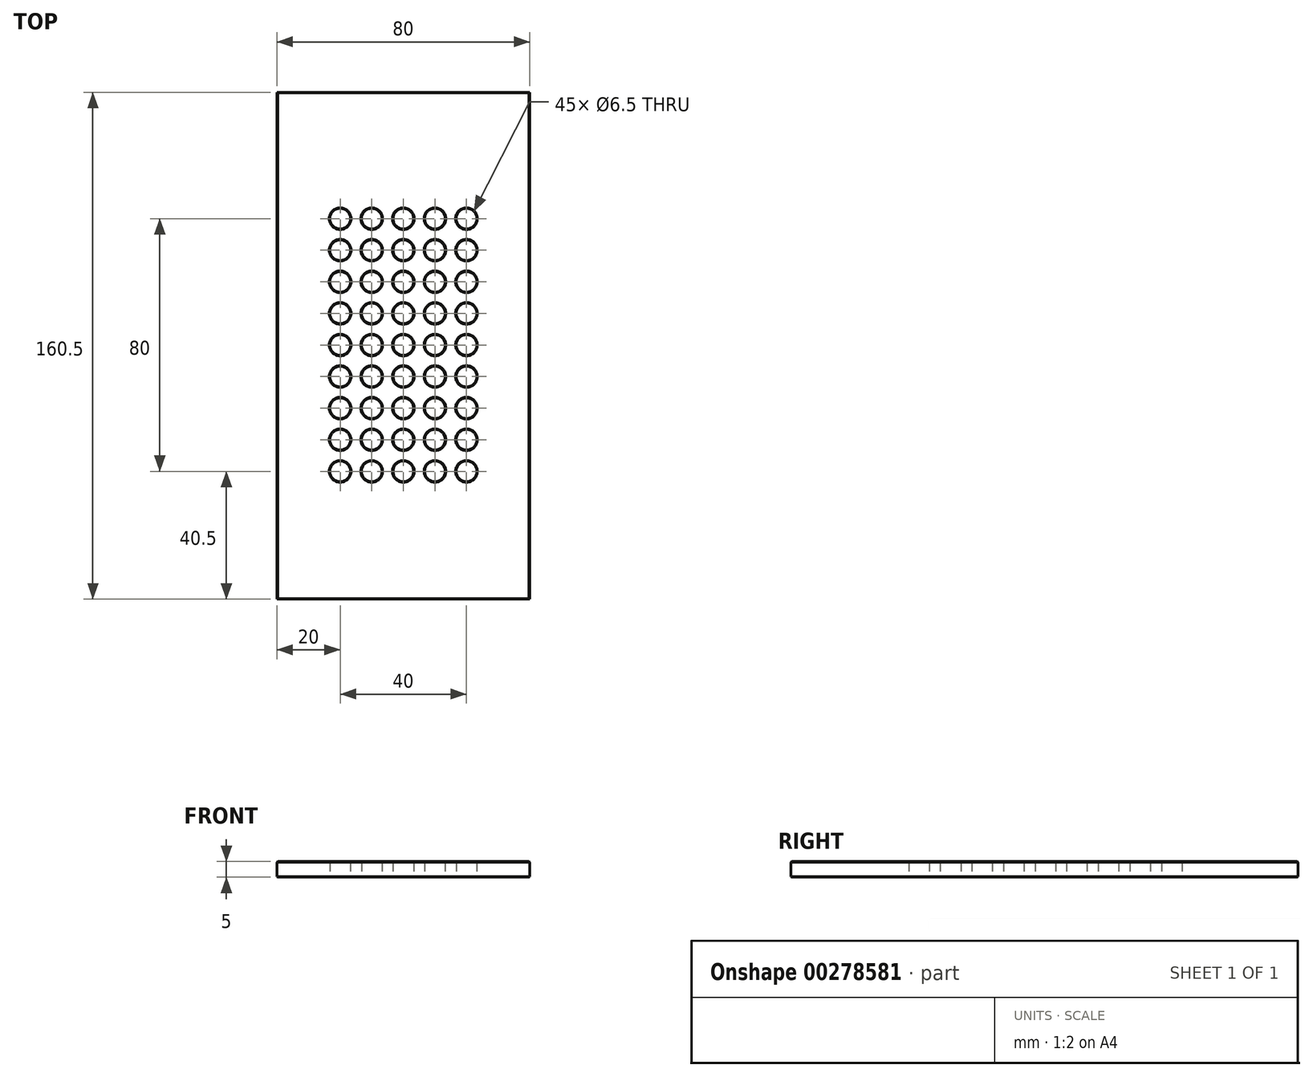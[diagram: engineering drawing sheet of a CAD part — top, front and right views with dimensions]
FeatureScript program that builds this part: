
annotation { "Feature Type Name" : "Feature", "Feature Type Description" : "" }
export const myFeature = defineFeature(function(context is Context, id is Id, definition is map)
    precondition{}
    {
        {
            var Q0;
            Q0=qCreatedBy(makeId("Top.planeOp"),FACE);
            var sketch = newSketch(context, id + "F0", { "sketchPlane" : qUnion([Q0])});
            skLineSegment(sketch, "E0.bottom", {"start": v(40, -80.25) * mm, "end": v(-40, -80.25) * mm});
            skLineSegment(sketch, "E0.top", {"start": v(40, 80.25) * mm, "end": v(-40, 80.25) * mm});
            skLineSegment(sketch, "E0.left", {"start": v(40, -80.25) * mm, "end": v(40, 80.25) * mm});
            skLineSegment(sketch, "E0.right", {"start": v(-40, -80.25) * mm, "end": v(-40, 80.25) * mm});
            skPoint(sketch, "E0.middle", {"position": v(0, 0) * mm});
            skLineSegment(sketch, "E1", {"start": v(-40, -50.25) * mm, "end": v(40, -50.25) * mm, "construction": true});
            skLineSegment(sketch, "E2", {"start": v(-40, 50.25) * mm, "end": v(40, 50.25) * mm, "construction": true});
            skLineSegment(sketch, "E3", {"start": v(0, 80.25) * mm, "end": v(0, -80.25) * mm, "construction": true});
            skLineSegment(sketch, "E4", {"start": v(10, 80.25) * mm, "end": v(10, -80.25) * mm, "construction": true});
            skLineSegment(sketch, "E5", {"start": v(-10, 80.25) * mm, "end": v(-10, -80.25) * mm, "construction": true});
            skCircle(sketch, "E6", {"center": v(-20, 40.25) * mm, "radius": 3.25 * mm});
            skLineSegment(sketch, "E7", {"start": v(20, 80.25) * mm, "end": v(20, -80.25) * mm, "construction": true});
            skLineSegment(sketch, "E8", {"start": v(-20, 80.25) * mm, "end": v(-20, -80.25) * mm, "construction": true});
            skLineSegment(sketch, "E9", {"start": v(-40, 70.25) * mm, "end": v(40, 70.25) * mm, "construction": true});
            skLineSegment(sketch, "E10", {"start": v(-40, 60.25) * mm, "end": v(40, 60.25) * mm, "construction": true});
            skLineSegment(sketch, "E11", {"start": v(-40, 40.25) * mm, "end": v(40, 40.25) * mm, "construction": true});
            skLineSegment(sketch, "E12", {"start": v(-40, 30.25) * mm, "end": v(40, 30.25) * mm, "construction": true});
            skLineSegment(sketch, "E13", {"start": v(-40, 20.25) * mm, "end": v(40, 20.25) * mm, "construction": true});
            skLineSegment(sketch, "E14", {"start": v(-40, 10.25) * mm, "end": v(40, 10.25) * mm, "construction": true});
            skCircle(sketch, "E15.0.1.0", {"center": v(-20, 30.25) * mm, "radius": 3.25 * mm});
            skCircle(sketch, "E15.0.2.0", {"center": v(-20, 20.25) * mm, "radius": 3.25 * mm});
            skCircle(sketch, "E15.0.3.0", {"center": v(-20, 10.25) * mm, "radius": 3.25 * mm});
            skCircle(sketch, "E15.0.4.0", {"center": v(-20, 0.25) * mm, "radius": 3.25 * mm});
            skCircle(sketch, "E15.0.5.0", {"center": v(-20, -9.75) * mm, "radius": 3.25 * mm});
            skCircle(sketch, "E15.0.6.0", {"center": v(-20, -19.75) * mm, "radius": 3.25 * mm});
            skCircle(sketch, "E15.0.7.0", {"center": v(-20, -29.75) * mm, "radius": 3.25 * mm});
            skCircle(sketch, "E15.0.8.0", {"center": v(-20, -39.75) * mm, "radius": 3.25 * mm});
            skCircle(sketch, "E15.1.0.0", {"center": v(-10, 40.25) * mm, "radius": 3.25 * mm});
            skCircle(sketch, "E15.1.1.0", {"center": v(-10, 30.25) * mm, "radius": 3.25 * mm});
            skCircle(sketch, "E15.1.2.0", {"center": v(-10, 20.25) * mm, "radius": 3.25 * mm});
            skCircle(sketch, "E15.1.3.0", {"center": v(-10, 10.25) * mm, "radius": 3.25 * mm});
            skCircle(sketch, "E15.1.4.0", {"center": v(-10, 0.25) * mm, "radius": 3.25 * mm});
            skCircle(sketch, "E15.1.5.0", {"center": v(-10, -9.75) * mm, "radius": 3.25 * mm});
            skCircle(sketch, "E15.1.6.0", {"center": v(-10, -19.75) * mm, "radius": 3.25 * mm});
            skCircle(sketch, "E15.1.7.0", {"center": v(-10, -29.75) * mm, "radius": 3.25 * mm});
            skCircle(sketch, "E15.1.8.0", {"center": v(-10, -39.75) * mm, "radius": 3.25 * mm});
            skCircle(sketch, "E15.2.0.0", {"center": v(0, 40.25) * mm, "radius": 3.25 * mm});
            skCircle(sketch, "E15.2.1.0", {"center": v(0, 30.25) * mm, "radius": 3.25 * mm});
            skCircle(sketch, "E15.2.2.0", {"center": v(0, 20.25) * mm, "radius": 3.25 * mm});
            skCircle(sketch, "E15.2.3.0", {"center": v(0, 10.25) * mm, "radius": 3.25 * mm});
            skCircle(sketch, "E15.2.4.0", {"center": v(0, 0.25) * mm, "radius": 3.25 * mm});
            skCircle(sketch, "E15.2.5.0", {"center": v(0, -9.75) * mm, "radius": 3.25 * mm});
            skCircle(sketch, "E15.2.6.0", {"center": v(0, -19.75) * mm, "radius": 3.25 * mm});
            skCircle(sketch, "E15.2.7.0", {"center": v(0, -29.75) * mm, "radius": 3.25 * mm});
            skCircle(sketch, "E15.2.8.0", {"center": v(0, -39.75) * mm, "radius": 3.25 * mm});
            skCircle(sketch, "E15.3.0.0", {"center": v(10, 40.25) * mm, "radius": 3.25 * mm});
            skCircle(sketch, "E15.3.1.0", {"center": v(10, 30.25) * mm, "radius": 3.25 * mm});
            skCircle(sketch, "E15.3.2.0", {"center": v(10, 20.25) * mm, "radius": 3.25 * mm});
            skCircle(sketch, "E15.3.3.0", {"center": v(10, 10.25) * mm, "radius": 3.25 * mm});
            skCircle(sketch, "E15.3.4.0", {"center": v(10, 0.25) * mm, "radius": 3.25 * mm});
            skCircle(sketch, "E15.3.5.0", {"center": v(10, -9.75) * mm, "radius": 3.25 * mm});
            skCircle(sketch, "E15.3.6.0", {"center": v(10, -19.75) * mm, "radius": 3.25 * mm});
            skCircle(sketch, "E15.3.7.0", {"center": v(10, -29.75) * mm, "radius": 3.25 * mm});
            skCircle(sketch, "E15.3.8.0", {"center": v(10, -39.75) * mm, "radius": 3.25 * mm});
            skCircle(sketch, "E15.4.0.0", {"center": v(20, 40.25) * mm, "radius": 3.25 * mm});
            skCircle(sketch, "E15.4.1.0", {"center": v(20, 30.25) * mm, "radius": 3.25 * mm});
            skCircle(sketch, "E15.4.2.0", {"center": v(20, 20.25) * mm, "radius": 3.25 * mm});
            skCircle(sketch, "E15.4.3.0", {"center": v(20, 10.25) * mm, "radius": 3.25 * mm});
            skCircle(sketch, "E15.4.4.0", {"center": v(20, 0.25) * mm, "radius": 3.25 * mm});
            skCircle(sketch, "E15.4.5.0", {"center": v(20, -9.75) * mm, "radius": 3.25 * mm});
            skCircle(sketch, "E15.4.6.0", {"center": v(20, -19.75) * mm, "radius": 3.25 * mm});
            skCircle(sketch, "E15.4.7.0", {"center": v(20, -29.75) * mm, "radius": 3.25 * mm});
            skCircle(sketch, "E15.4.8.0", {"center": v(20, -39.75) * mm, "radius": 3.25 * mm});
            skLineSegment(sketch, "E15.direction1", {"start": v(-20, 40.25) * mm, "end": v(-10, 40.25) * mm, "construction": true});
            skLineSegment(sketch, "E15.direction2", {"start": v(-20, 40.25) * mm, "end": v(-20, 30.25) * mm, "construction": true});
            skSolve(sketch);
        }
        {
            var Q0;
            Q0=makeQuery(id+"F0.imprint","IMPRINT",FACE,{"disambiguationData":[TD([[makeQuery(id+"F0.imprint","IMPRINT",EDGE,{"derivedFrom":sQuery(id+"F0.wireOp",EDGE,"E0.bottom")}),-1.0]])]});
            extrude(context, id + "F1", {"entities" : qUnion([Q0]), "depth" : 5 * mm});
        }
        {
            var Q0;
            Q0=makeQuery(id+"F1.opExtrude","CAP_EDGE",EDGE,{"disambiguationData":[OSD([sQuery(id+"F0.wireOp",EDGE,"E6")])],"isStart":false});
            var Q1;
            Q1=makeQuery(id+"F1.opExtrude","CAP_EDGE",EDGE,{"disambiguationData":[OSD([sQuery(id+"F0.wireOp",EDGE,"E15.1.0.0")])],"isStart":false});
            var Q2;
            Q2=makeQuery(id+"F1.opExtrude","CAP_EDGE",EDGE,{"disambiguationData":[OSD([sQuery(id+"F0.wireOp",EDGE,"E15.2.0.0")])],"isStart":false});
            var Q3;
            Q3=makeQuery(id+"F1.opExtrude","CAP_EDGE",EDGE,{"disambiguationData":[OSD([sQuery(id+"F0.wireOp",EDGE,"E15.3.0.0")])],"isStart":false});
            var Q4;
            Q4=makeQuery(id+"F1.opExtrude","CAP_EDGE",EDGE,{"disambiguationData":[OSD([sQuery(id+"F0.wireOp",EDGE,"E15.4.0.0")])],"isStart":false});
            var Q5;
            Q5=makeQuery(id+"F1.opExtrude","CAP_EDGE",EDGE,{"disambiguationData":[OSD([sQuery(id+"F0.wireOp",EDGE,"E15.4.1.0")])],"isStart":false});
            var Q6;
            Q6=makeQuery(id+"F1.opExtrude","CAP_EDGE",EDGE,{"disambiguationData":[OSD([sQuery(id+"F0.wireOp",EDGE,"E15.3.2.0")])],"isStart":false});
            var Q7;
            Q7=makeQuery(id+"F1.opExtrude","CAP_EDGE",EDGE,{"disambiguationData":[OSD([sQuery(id+"F0.wireOp",EDGE,"E15.3.1.0")])],"isStart":false});
            var Q8;
            Q8=makeQuery(id+"F1.opExtrude","CAP_EDGE",EDGE,{"disambiguationData":[OSD([sQuery(id+"F0.wireOp",EDGE,"E15.2.1.0")])],"isStart":false});
            var Q9;
            Q9=makeQuery(id+"F1.opExtrude","CAP_EDGE",EDGE,{"disambiguationData":[OSD([sQuery(id+"F0.wireOp",EDGE,"E15.2.2.0")])],"isStart":false});
            var Q10;
            Q10=makeQuery(id+"F1.opExtrude","CAP_EDGE",EDGE,{"disambiguationData":[OSD([sQuery(id+"F0.wireOp",EDGE,"E15.1.3.0")])],"isStart":false});
            var Q11;
            Q11=makeQuery(id+"F1.opExtrude","CAP_EDGE",EDGE,{"disambiguationData":[OSD([sQuery(id+"F0.wireOp",EDGE,"E15.1.2.0")])],"isStart":false});
            var Q12;
            Q12=makeQuery(id+"F1.opExtrude","CAP_EDGE",EDGE,{"disambiguationData":[OSD([sQuery(id+"F0.wireOp",EDGE,"E15.1.1.0")])],"isStart":false});
            var Q13;
            Q13=makeQuery(id+"F1.opExtrude","CAP_EDGE",EDGE,{"disambiguationData":[OSD([sQuery(id+"F0.wireOp",EDGE,"E15.0.2.0")])],"isStart":false});
            var Q14;
            Q14=makeQuery(id+"F1.opExtrude","CAP_EDGE",EDGE,{"disambiguationData":[OSD([sQuery(id+"F0.wireOp",EDGE,"E15.0.1.0")])],"isStart":false});
            var Q15;
            Q15=makeQuery(id+"F1.opExtrude","CAP_EDGE",EDGE,{"disambiguationData":[OSD([sQuery(id+"F0.wireOp",EDGE,"E15.0.4.0")])],"isStart":false});
            var Q16;
            Q16=makeQuery(id+"F1.opExtrude","CAP_EDGE",EDGE,{"disambiguationData":[OSD([sQuery(id+"F0.wireOp",EDGE,"E15.0.3.0")])],"isStart":false});
            var Q17;
            Q17=makeQuery(id+"F1.opExtrude","CAP_EDGE",EDGE,{"disambiguationData":[OSD([sQuery(id+"F0.wireOp",EDGE,"E15.2.3.0")])],"isStart":false});
            var Q18;
            Q18=makeQuery(id+"F1.opExtrude","CAP_EDGE",EDGE,{"disambiguationData":[OSD([sQuery(id+"F0.wireOp",EDGE,"E15.1.4.0")])],"isStart":false});
            var Q19;
            Q19=makeQuery(id+"F1.opExtrude","CAP_EDGE",EDGE,{"disambiguationData":[OSD([sQuery(id+"F0.wireOp",EDGE,"E15.2.5.0")])],"isStart":false});
            var Q20;
            Q20=makeQuery(id+"F1.opExtrude","CAP_EDGE",EDGE,{"disambiguationData":[OSD([sQuery(id+"F0.wireOp",EDGE,"E15.3.4.0")])],"isStart":false});
            var Q21;
            Q21=makeQuery(id+"F1.opExtrude","CAP_EDGE",EDGE,{"disambiguationData":[OSD([sQuery(id+"F0.wireOp",EDGE,"E15.4.2.0")])],"isStart":false});
            var Q22;
            Q22=makeQuery(id+"F1.opExtrude","CAP_EDGE",EDGE,{"disambiguationData":[OSD([sQuery(id+"F0.wireOp",EDGE,"E15.4.3.0")])],"isStart":false});
            var Q23;
            Q23=makeQuery(id+"F1.opExtrude","CAP_EDGE",EDGE,{"disambiguationData":[OSD([sQuery(id+"F0.wireOp",EDGE,"E15.4.4.0")])],"isStart":false});
            var Q24;
            Q24=makeQuery(id+"F1.opExtrude","CAP_EDGE",EDGE,{"disambiguationData":[OSD([sQuery(id+"F0.wireOp",EDGE,"E15.4.5.0")])],"isStart":false});
            var Q25;
            Q25=makeQuery(id+"F1.opExtrude","CAP_EDGE",EDGE,{"disambiguationData":[OSD([sQuery(id+"F0.wireOp",EDGE,"E15.3.3.0")])],"isStart":false});
            var Q26;
            Q26=makeQuery(id+"F1.opExtrude","CAP_EDGE",EDGE,{"disambiguationData":[OSD([sQuery(id+"F0.wireOp",EDGE,"E15.2.4.0")])],"isStart":false});
            var Q27;
            Q27=makeQuery(id+"F1.opExtrude","CAP_EDGE",EDGE,{"disambiguationData":[OSD([sQuery(id+"F0.wireOp",EDGE,"E15.1.5.0")])],"isStart":false});
            var Q28;
            Q28=makeQuery(id+"F1.opExtrude","CAP_EDGE",EDGE,{"disambiguationData":[OSD([sQuery(id+"F0.wireOp",EDGE,"E15.0.5.0")])],"isStart":false});
            var Q29;
            Q29=makeQuery(id+"F1.opExtrude","CAP_EDGE",EDGE,{"disambiguationData":[OSD([sQuery(id+"F0.wireOp",EDGE,"E15.3.6.0")])],"isStart":false});
            var Q30;
            Q30=makeQuery(id+"F1.opExtrude","CAP_EDGE",EDGE,{"disambiguationData":[OSD([sQuery(id+"F0.wireOp",EDGE,"E15.3.5.0")])],"isStart":false});
            var Q31;
            Q31=makeQuery(id+"F1.opExtrude","CAP_EDGE",EDGE,{"disambiguationData":[OSD([sQuery(id+"F0.wireOp",EDGE,"E15.4.6.0")])],"isStart":false});
            var Q32;
            Q32=makeQuery(id+"F1.opExtrude","CAP_EDGE",EDGE,{"disambiguationData":[OSD([sQuery(id+"F0.wireOp",EDGE,"E15.2.6.0")])],"isStart":false});
            var Q33;
            Q33=makeQuery(id+"F1.opExtrude","CAP_EDGE",EDGE,{"disambiguationData":[OSD([sQuery(id+"F0.wireOp",EDGE,"E15.1.6.0")])],"isStart":false});
            var Q34;
            Q34=makeQuery(id+"F1.opExtrude","CAP_EDGE",EDGE,{"disambiguationData":[OSD([sQuery(id+"F0.wireOp",EDGE,"E15.0.6.0")])],"isStart":false});
            var Q35;
            Q35=makeQuery(id+"F1.opExtrude","CAP_EDGE",EDGE,{"disambiguationData":[OSD([sQuery(id+"F0.wireOp",EDGE,"E15.1.7.0")])],"isStart":false});
            var Q36;
            Q36=makeQuery(id+"F1.opExtrude","CAP_EDGE",EDGE,{"disambiguationData":[OSD([sQuery(id+"F0.wireOp",EDGE,"E15.0.7.0")])],"isStart":false});
            var Q37;
            Q37=makeQuery(id+"F1.opExtrude","CAP_EDGE",EDGE,{"disambiguationData":[OSD([sQuery(id+"F0.wireOp",EDGE,"E15.2.7.0")])],"isStart":false});
            var Q38;
            Q38=makeQuery(id+"F1.opExtrude","CAP_EDGE",EDGE,{"disambiguationData":[OSD([sQuery(id+"F0.wireOp",EDGE,"E15.3.7.0")])],"isStart":false});
            var Q39;
            Q39=makeQuery(id+"F1.opExtrude","CAP_EDGE",EDGE,{"disambiguationData":[OSD([sQuery(id+"F0.wireOp",EDGE,"E15.4.7.0")])],"isStart":false});
            var Q40;
            Q40=makeQuery(id+"F1.opExtrude","CAP_EDGE",EDGE,{"disambiguationData":[OSD([sQuery(id+"F0.wireOp",EDGE,"E15.4.8.0")])],"isStart":false});
            var Q41;
            Q41=makeQuery(id+"F1.opExtrude","CAP_EDGE",EDGE,{"disambiguationData":[OSD([sQuery(id+"F0.wireOp",EDGE,"E15.3.8.0")])],"isStart":false});
            var Q42;
            Q42=makeQuery(id+"F1.opExtrude","CAP_EDGE",EDGE,{"disambiguationData":[OSD([sQuery(id+"F0.wireOp",EDGE,"E15.2.8.0")])],"isStart":false});
            var Q43;
            Q43=makeQuery(id+"F1.opExtrude","CAP_EDGE",EDGE,{"disambiguationData":[OSD([sQuery(id+"F0.wireOp",EDGE,"E15.1.8.0")])],"isStart":false});
            var Q44;
            Q44=makeQuery(id+"F1.opExtrude","CAP_EDGE",EDGE,{"disambiguationData":[OSD([sQuery(id+"F0.wireOp",EDGE,"E15.0.8.0")])],"isStart":false});
            var Q45;
            Q45=makeQuery(id+"F1.opExtrude","CAP_EDGE",EDGE,{"disambiguationData":[OSD([sQuery(id+"F0.wireOp",EDGE,"E0.left")])],"isStart":false});
            var Q46;
            Q46=makeQuery(id+"F1.opExtrude","CAP_EDGE",EDGE,{"disambiguationData":[OSD([sQuery(id+"F0.wireOp",EDGE,"E0.left")])],"isStart":true});
            var Q47;
            Q47=makeQuery(id+"F1.opExtrude","CAP_EDGE",EDGE,{"disambiguationData":[OSD([sQuery(id+"F0.wireOp",EDGE,"E0.top")])],"isStart":false});
            var Q48;
            Q48=makeQuery(id+"F1.opExtrude","CAP_EDGE",EDGE,{"disambiguationData":[OSD([sQuery(id+"F0.wireOp",EDGE,"E0.right")])],"isStart":false});
            var Q49;
            Q49=makeQuery(id+"F1.opExtrude","CAP_EDGE",EDGE,{"disambiguationData":[OSD([sQuery(id+"F0.wireOp",EDGE,"E0.bottom")])],"isStart":false});
            var Q50;
            Q50=makeQuery(id+"F1.opExtrude","CAP_EDGE",EDGE,{"disambiguationData":[OSD([sQuery(id+"F0.wireOp",EDGE,"E0.bottom")])],"isStart":true});
            var Q51;
            Q51=makeQuery(id+"F1.opExtrude","CAP_FACE",FACE,{"disambiguationData":[OSD([sQuery(id+"F0.wireOp",EDGE,"E0.bottom"),sQuery(id+"F0.wireOp",EDGE,"E0.top"),sQuery(id+"F0.wireOp",EDGE,"E0.left"),sQuery(id+"F0.wireOp",EDGE,"E0.right"),sQuery(id+"F0.wireOp",EDGE,"E6"),sQuery(id+"F0.wireOp",EDGE,"E15.0.1.0"),sQuery(id+"F0.wireOp",EDGE,"E15.0.2.0"),sQuery(id+"F0.wireOp",EDGE,"E15.0.3.0"),sQuery(id+"F0.wireOp",EDGE,"E15.0.4.0"),sQuery(id+"F0.wireOp",EDGE,"E15.0.5.0"),sQuery(id+"F0.wireOp",EDGE,"E15.0.6.0"),sQuery(id+"F0.wireOp",EDGE,"E15.0.7.0"),sQuery(id+"F0.wireOp",EDGE,"E15.0.8.0"),sQuery(id+"F0.wireOp",EDGE,"E15.1.0.0"),sQuery(id+"F0.wireOp",EDGE,"E15.1.1.0"),sQuery(id+"F0.wireOp",EDGE,"E15.1.2.0"),sQuery(id+"F0.wireOp",EDGE,"E15.1.3.0"),sQuery(id+"F0.wireOp",EDGE,"E15.1.4.0"),sQuery(id+"F0.wireOp",EDGE,"E15.1.5.0"),sQuery(id+"F0.wireOp",EDGE,"E15.1.6.0"),sQuery(id+"F0.wireOp",EDGE,"E15.1.7.0"),sQuery(id+"F0.wireOp",EDGE,"E15.1.8.0"),sQuery(id+"F0.wireOp",EDGE,"E15.2.0.0"),sQuery(id+"F0.wireOp",EDGE,"E15.2.1.0"),sQuery(id+"F0.wireOp",EDGE,"E15.2.2.0"),sQuery(id+"F0.wireOp",EDGE,"E15.2.3.0"),sQuery(id+"F0.wireOp",EDGE,"E15.2.4.0"),sQuery(id+"F0.wireOp",EDGE,"E15.2.5.0"),sQuery(id+"F0.wireOp",EDGE,"E15.2.6.0"),sQuery(id+"F0.wireOp",EDGE,"E15.2.7.0"),sQuery(id+"F0.wireOp",EDGE,"E15.2.8.0"),sQuery(id+"F0.wireOp",EDGE,"E15.3.0.0"),sQuery(id+"F0.wireOp",EDGE,"E15.3.1.0"),sQuery(id+"F0.wireOp",EDGE,"E15.3.2.0"),sQuery(id+"F0.wireOp",EDGE,"E15.3.3.0"),sQuery(id+"F0.wireOp",EDGE,"E15.3.4.0"),sQuery(id+"F0.wireOp",EDGE,"E15.3.5.0"),sQuery(id+"F0.wireOp",EDGE,"E15.3.6.0"),sQuery(id+"F0.wireOp",EDGE,"E15.3.7.0"),sQuery(id+"F0.wireOp",EDGE,"E15.3.8.0"),sQuery(id+"F0.wireOp",EDGE,"E15.4.0.0"),sQuery(id+"F0.wireOp",EDGE,"E15.4.1.0"),sQuery(id+"F0.wireOp",EDGE,"E15.4.2.0"),sQuery(id+"F0.wireOp",EDGE,"E15.4.3.0"),sQuery(id+"F0.wireOp",EDGE,"E15.4.4.0"),sQuery(id+"F0.wireOp",EDGE,"E15.4.5.0"),sQuery(id+"F0.wireOp",EDGE,"E15.4.6.0"),sQuery(id+"F0.wireOp",EDGE,"E15.4.7.0"),sQuery(id+"F0.wireOp",EDGE,"E15.4.8.0")])],"isStart":true});
            var Q52;
            Q52=makeQuery(id+"F1.opExtrude","CAP_EDGE",EDGE,{"disambiguationData":[OSD([sQuery(id+"F0.wireOp",EDGE,"E0.top")])],"isStart":true});
            var Q53;
            Q53=makeQuery(id+"F1.opExtrude","CAP_EDGE",EDGE,{"disambiguationData":[OSD([sQuery(id+"F0.wireOp",EDGE,"E0.right")])],"isStart":true});
            chamfer(context, id + "F2", {"entities" : qUnion([Q0, Q1, Q2, Q3, Q4, Q5, Q6, Q7, Q8, Q9, Q10, Q11, Q12, Q13, Q14, Q15, Q16, Q17, Q18, Q19, Q20, Q21, Q22, Q23, Q24, Q25, Q26, Q27, Q28, Q29, Q30, Q31, Q32, Q33, Q34, Q35, Q36, Q37, Q38, Q39, Q40, Q41, Q42, Q43, Q44, Q45, Q46, Q47, Q48, Q49, Q50, Q51, Q52, Q53]), "width" : 0.2 * mm, "tangentPropagation" : true});
        }
    });
